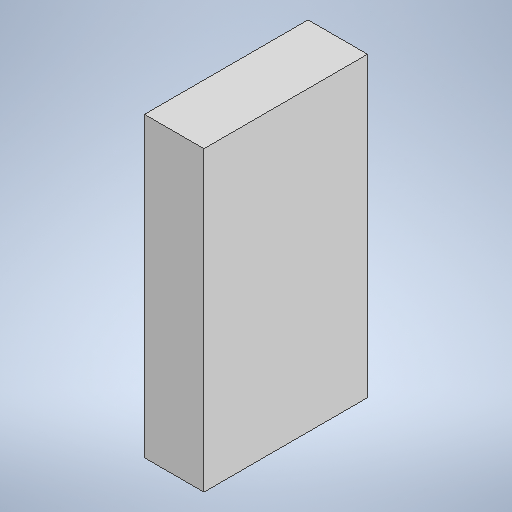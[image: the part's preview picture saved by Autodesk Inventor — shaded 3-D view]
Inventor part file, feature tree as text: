
AUTODESK INVENTOR PART (.ipt)
format: ipt  version: 2025 (Build 290162010, 162A)  size: 207,360 bytes
history: native  units: mm
features: extrude x1, sketch x1
ambient origin geometry x8: Origin, YZ Plane, XZ Plane, XY Plane, X Axis, Y Axis, Z Axis, Center Point
bodies: Solid1 (feature_tree)
feature tree (2):
  extrude  "Extrusion1"  Depth=400.0mm
  sketch  "Sketch1"  dims[d0=1100.0mm d1=400.0mm d2=2000.0mm d3=0.0mm]
